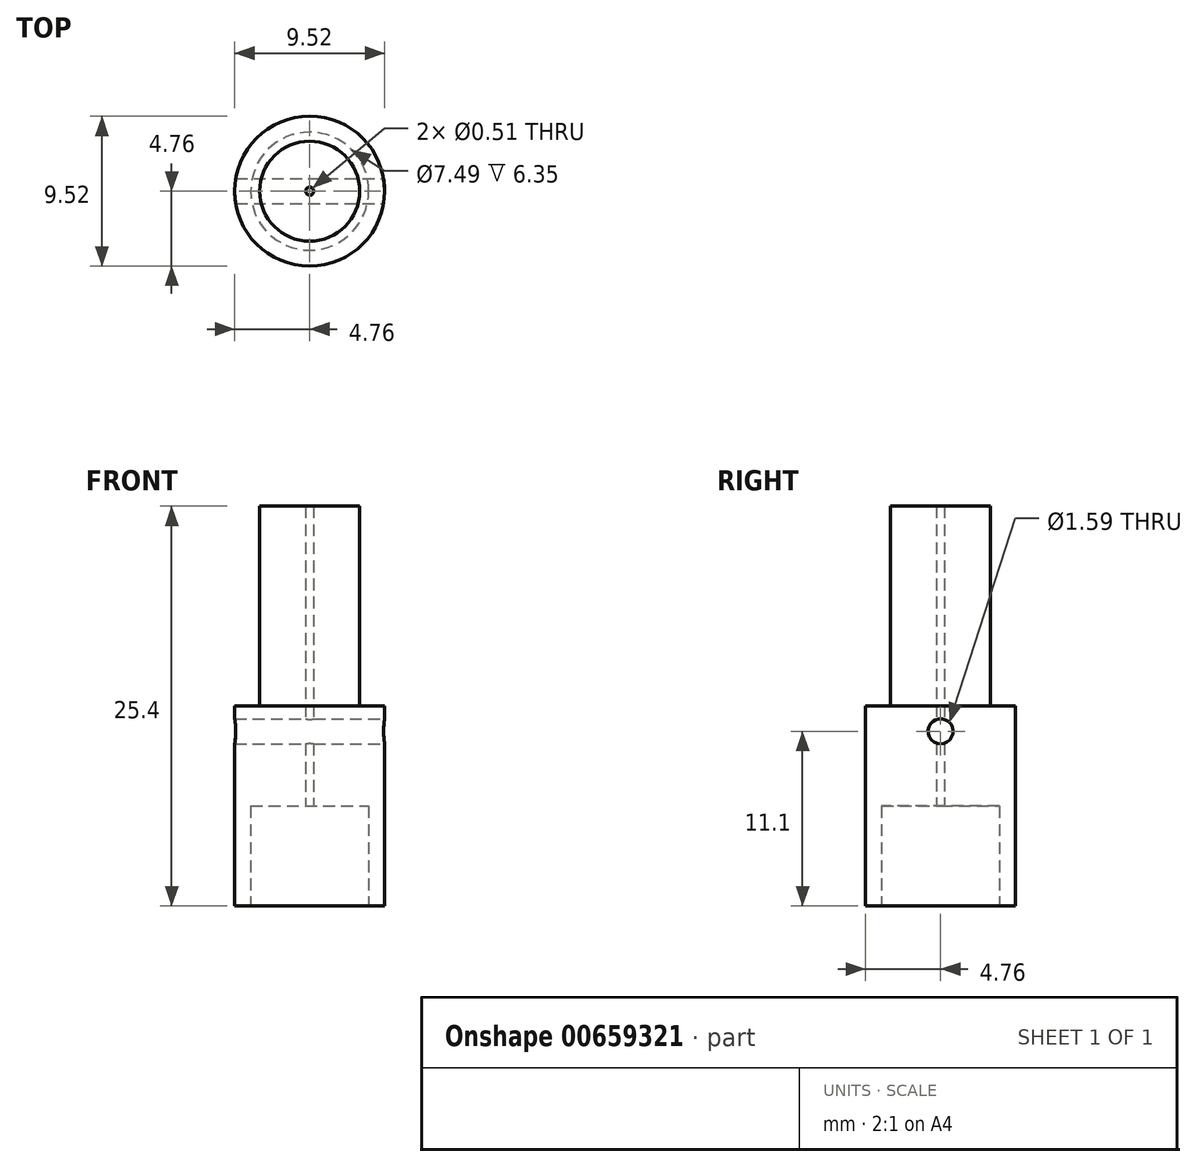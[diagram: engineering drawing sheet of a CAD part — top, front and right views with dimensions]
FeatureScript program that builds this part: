
annotation { "Feature Type Name" : "Feature", "Feature Type Description" : "" }
export const myFeature = defineFeature(function(context is Context, id is Id, definition is map)
    precondition{}
    {
        {
            var Q0;
            Q0=qCreatedBy(makeId("Top.planeOp"),FACE);
            var sketch = newSketch(context, id + "F0", { "sketchPlane" : qUnion([Q0])});
            skCircle(sketch, "E0", {"center": v(0, 0) * mm, "radius": 3.18 * mm});
            skSolve(sketch);
        }
        {
            var Q0;
            Q0 = qSketchRegion(id + "F0", true);
            extrude(context, id + "F1", {"entities" : qUnion([Q0]), "depth" : 12.7 * mm, "offsetDistance" : 25.4 * mm});
        }
        {
            var Q0;
            Q0=makeQuery(id+"F1.opExtrude","CAP_FACE",FACE,{"disambiguationData":[OSD([sQuery(id+"F0.wireOp",EDGE,"E0")])],"isStart":true});
            var sketch = newSketch(context, id + "F2", { "sketchPlane" : qUnion([Q0])});
            skCircle(sketch, "E1", {"center": v(0, 0) * mm, "radius": 4.76 * mm});
            skSolve(sketch);
        }
        {
            var Q0;
            Q0=makeQuery(id+"F2.imprint","IMPRINT",FACE,{"disambiguationData":[TD([[makeQuery(id+"F2.imprint","IMPRINT",EDGE,{"derivedFrom":sQuery(id+"F2.wireOp",EDGE,"E1")}),1.0]])]});
            var Q1;
            Q1=makeQuery(id+"F2.imprint","IMPRINT",FACE,{"disambiguationData":[TD([[makeQuery(id+"F2.imprint","IMPRINT",EDGE,{"derivedFrom":makeQuery(id+"F1.opExtrude","CAP_EDGE",EDGE,{"disambiguationData":[OSD([sQuery(id+"F0.wireOp",EDGE,"E0")])],"isStart":true})}),-1.0]])]});
            extrude(context, id + "F3", {"entities" : qUnion([Q0, Q1]), "operationType" : NewBodyOperationType.ADD, "depth" : 12.7 * mm, "offsetDistance" : 25.4 * mm});
        }
        {
            var Q0;
            Q0=makeQuery(id+"F3.opExtrude","CAP_FACE",FACE,{"disambiguationData":[OSD([sQuery(id+"F2.wireOp",EDGE,"E1")])],"isStart":false});
            var sketch = newSketch(context, id + "F4", { "sketchPlane" : qUnion([Q0])});
            skCircle(sketch, "E2", {"center": v(0, 0) * mm, "radius": 0.25 * mm});
            skSolve(sketch);
        }
        {
            var Q0;
            Q0 = qSketchRegion(id + "F4", true);
            extrude(context, id + "F5", {"entities" : qUnion([Q0]), "operationType" : NewBodyOperationType.REMOVE, "oppositeDirection" : true, "depth" : 25.4 * mm, "offsetDistance" : 25.4 * mm});
        }
        {
            var Q0;
            Q0=makeQuery(id+"F3.opExtrude","CAP_FACE",FACE,{"disambiguationData":[OSD([sQuery(id+"F2.wireOp",EDGE,"E1")])],"isStart":false});
            var sketch = newSketch(context, id + "F6", { "sketchPlane" : qUnion([Q0])});
            skCircle(sketch, "E3", {"center": v(0, 0) * mm, "radius": 3.75 * mm});
            skSolve(sketch);
        }
        {
            var Q0;
            Q0=makeQuery(id+"F6.imprint","IMPRINT",FACE,{"disambiguationData":[TD([[makeQuery(id+"F6.imprint","IMPRINT",EDGE,{"derivedFrom":sQuery(id+"F6.wireOp",EDGE,"E3")}),1.0]])]});
            extrude(context, id + "F7", {"entities" : qUnion([Q0]), "operationType" : NewBodyOperationType.REMOVE, "oppositeDirection" : true, "depth" : 6.35 * mm, "offsetDistance" : 25.4 * mm});
        }
        {
            var Q0;
            Q0=qCreatedBy(makeId("Right.planeOp"),FACE);
            var sketch = newSketch(context, id + "F8", { "sketchPlane" : qUnion([Q0])});
            skCircle(sketch, "E4", {"center": v(0, -1.6) * mm, "radius": 0.8 * mm});
            skSolve(sketch);
        }
        {
            var Q0;
            Q0 = qSketchRegion(id + "F8", true);
            extrude(context, id + "F9", {"entities" : qUnion([Q0]), "operationType" : NewBodyOperationType.REMOVE, "endBound" : BoundingType.THROUGH_ALL, "oppositeDirection" : true, "depth" : 25.4 * mm, "offsetDistance" : 25.4 * mm, "hasSecondDirection" : true, "secondDirectionBound" : SecondDirectionBoundingType.THROUGH_ALL, "secondDirectionOppositeDirection" : false, "secondDirectionDepth" : 25.4 * mm});
        }
    });
